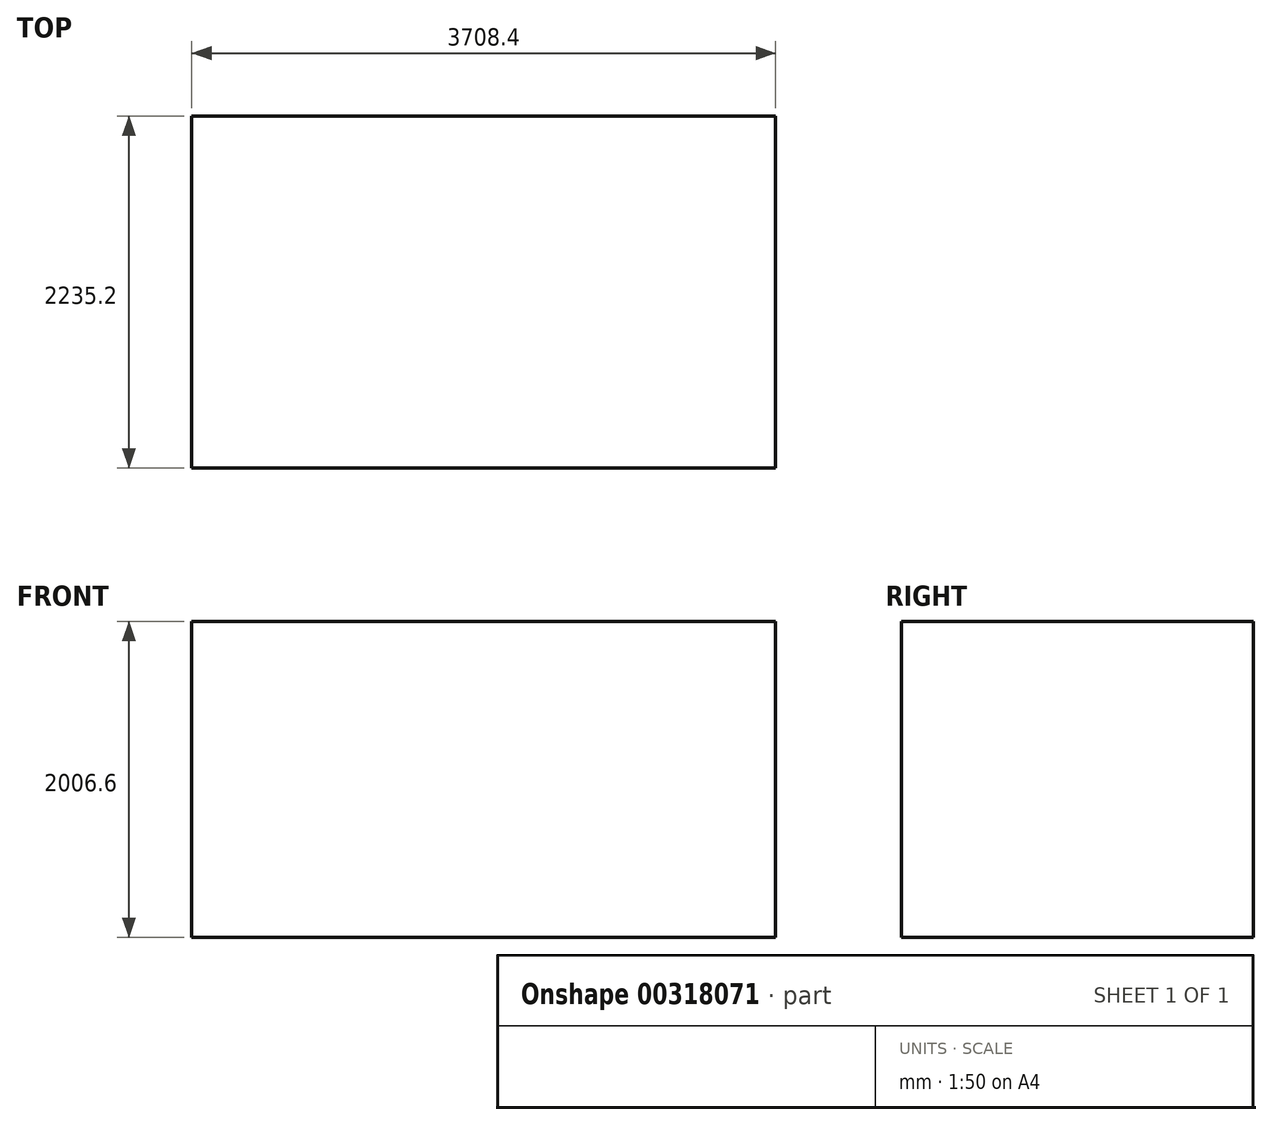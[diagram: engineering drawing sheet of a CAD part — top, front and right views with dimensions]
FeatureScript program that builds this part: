
annotation { "Feature Type Name" : "Feature", "Feature Type Description" : "" }
export const myFeature = defineFeature(function(context is Context, id is Id, definition is map)
    precondition{}
    {
        {
            var Q0;
            Q0=qCreatedBy(makeId("Front.planeOp"),FACE);
            var sketch = newSketch(context, id + "F0", { "sketchPlane" : qUnion([Q0])});
            skLineSegment(sketch, "E0.bottom", {"start": v(-3708.4, 2006.6) * mm, "end": v(0, 2006.6) * mm});
            skLineSegment(sketch, "E0.top", {"start": v(-3708.4, 0) * mm, "end": v(0, 0) * mm});
            skLineSegment(sketch, "E0.left", {"start": v(-3708.4, 2006.6) * mm, "end": v(-3708.4, 0) * mm});
            skLineSegment(sketch, "E0.right", {"start": v(0, 2006.6) * mm, "end": v(0, 0) * mm});
            skSolve(sketch);
        }
        {
            var Q0;
            Q0 = qSketchRegion(id + "F0", true);
            extrude(context, id + "F1", {"entities" : qUnion([Q0]), "depth" : 2235.2 * mm});
        }
    });
